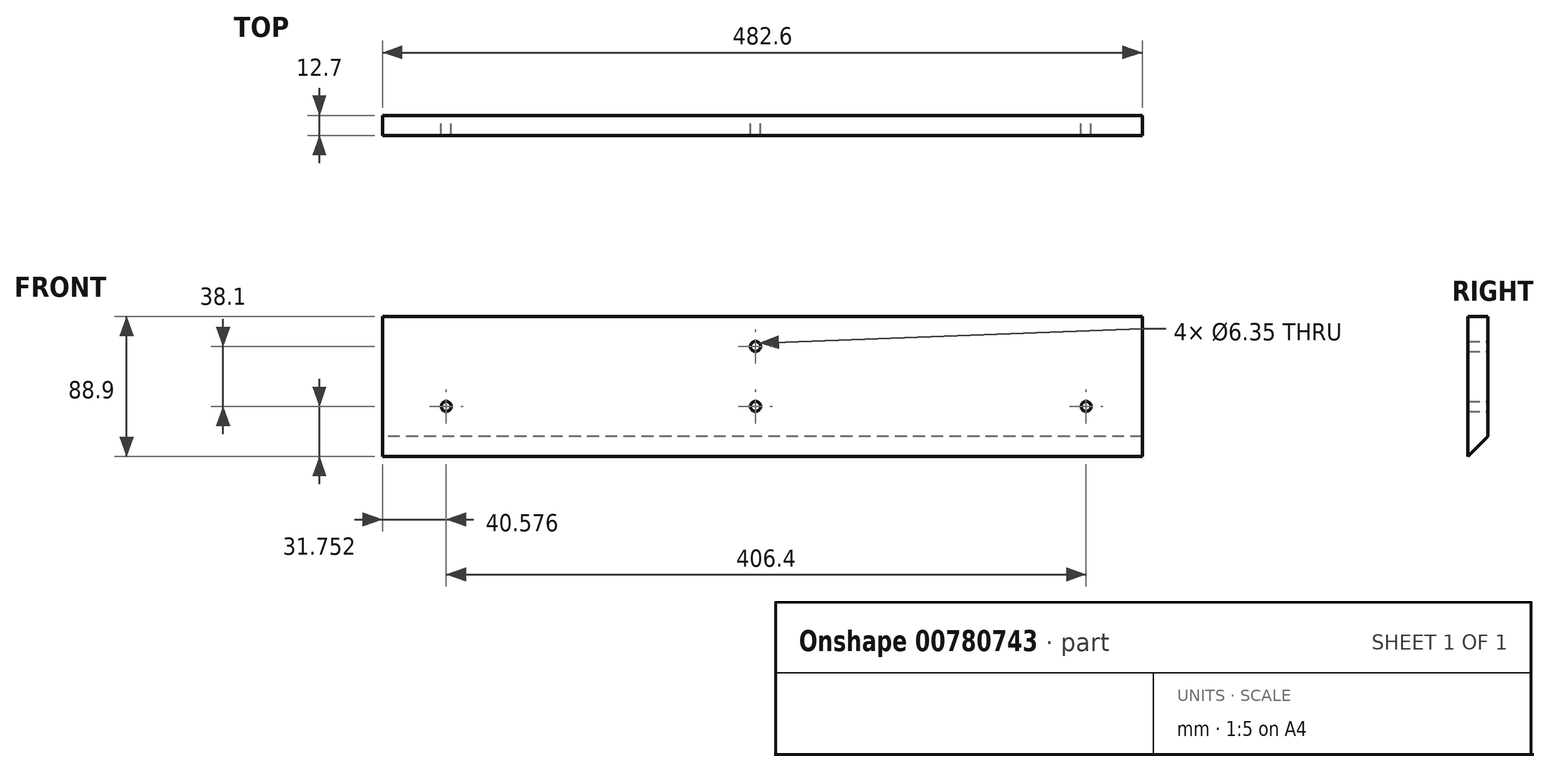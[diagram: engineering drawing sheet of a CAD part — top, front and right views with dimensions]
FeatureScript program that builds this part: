
annotation { "Feature Type Name" : "Feature", "Feature Type Description" : "" }
export const myFeature = defineFeature(function(context is Context, id is Id, definition is map)
    precondition{}
    {
        {
            var Q0;
            Q0=qCreatedBy(makeId("Right.planeOp"),FACE);
            var sketch = newSketch(context, id + "F0", { "sketchPlane" : qUnion([Q0])});
            skLineSegment(sketch, "E0", {"start": v(-6.88, 81.95) * mm, "end": v(5.82, 81.95) * mm});
            skLineSegment(sketch, "E1", {"start": v(5.82, 81.95) * mm, "end": v(5.82, 5.75) * mm});
            skLineSegment(sketch, "E2", {"start": v(5.82, 5.75) * mm, "end": v(-6.88, -6.95) * mm});
            skLineSegment(sketch, "E3", {"start": v(-6.88, -6.95) * mm, "end": v(-6.88, 81.95) * mm});
            skSolve(sketch);
        }
        {
            var Q0;
            Q0=makeQuery(id+"F0.imprint","IMPRINT",FACE,{"disambiguationData":[TD([[makeQuery(id+"F0.imprint","IMPRINT",EDGE,{"derivedFrom":sQuery(id+"F0.wireOp",EDGE,"E0")}),-1.0]])]});
            extrude(context, id + "F1", {"entities" : qUnion([Q0]), "depth" : 482.6 * mm, "offsetDistance" : 25.4 * mm});
        }
        {
            var Q0;
            Q0=makeQuery(id+"F1.opExtrude","SWEPT_FACE",FACE,{"disambiguationData":[OSD([sQuery(id+"F0.wireOp",EDGE,"E1")])]});
            var sketch = newSketch(context, id + "F2", { "sketchPlane" : qUnion([Q0])});
            skPoint(sketch, "E4", {"position": v(-237, 62.9) * mm});
            skPoint(sketch, "E5", {"position": v(-237, 24.8) * mm});
            skPoint(sketch, "E6", {"position": v(-446.98, 24.8) * mm});
            skPoint(sketch, "E7", {"position": v(-40.58, 24.8) * mm});
            skCircle(sketch, "E8", {"center": v(-40.58, 24.8) * mm, "radius": 3.18 * mm});
            skCircle(sketch, "E9", {"center": v(-237, 24.8) * mm, "radius": 3.18 * mm});
            skCircle(sketch, "E10", {"center": v(-237, 62.9) * mm, "radius": 3.18 * mm});
            skCircle(sketch, "E11", {"center": v(-446.98, 24.8) * mm, "radius": 3.18 * mm});
            skSolve(sketch);
        }
        {
            var Q0;
            Q0=makeQuery(id+"F2.imprint","IMPRINT",FACE,{"disambiguationData":[TD([[makeQuery(id+"F2.imprint","IMPRINT",EDGE,{"derivedFrom":sQuery(id+"F2.wireOp",EDGE,"E8")}),1.0]])]});
            var Q1;
            Q1=makeQuery(id+"F2.imprint","IMPRINT",FACE,{"disambiguationData":[TD([[makeQuery(id+"F2.imprint","IMPRINT",EDGE,{"derivedFrom":sQuery(id+"F2.wireOp",EDGE,"E9")}),1.0]])]});
            var Q2;
            Q2=makeQuery(id+"F2.imprint","IMPRINT",FACE,{"disambiguationData":[TD([[makeQuery(id+"F2.imprint","IMPRINT",EDGE,{"derivedFrom":sQuery(id+"F2.wireOp",EDGE,"E10")}),1.0]])]});
            var Q3;
            Q3=makeQuery(id+"F2.imprint","IMPRINT",FACE,{"disambiguationData":[TD([[makeQuery(id+"F2.imprint","IMPRINT",EDGE,{"derivedFrom":sQuery(id+"F2.wireOp",EDGE,"E11")}),1.0]])]});
            extrude(context, id + "F3", {"entities" : qUnion([Q0, Q1, Q2, Q3]), "operationType" : NewBodyOperationType.REMOVE, "oppositeDirection" : true, "depth" : 12.7 * mm, "offsetDistance" : 25.4 * mm});
        }
    });
